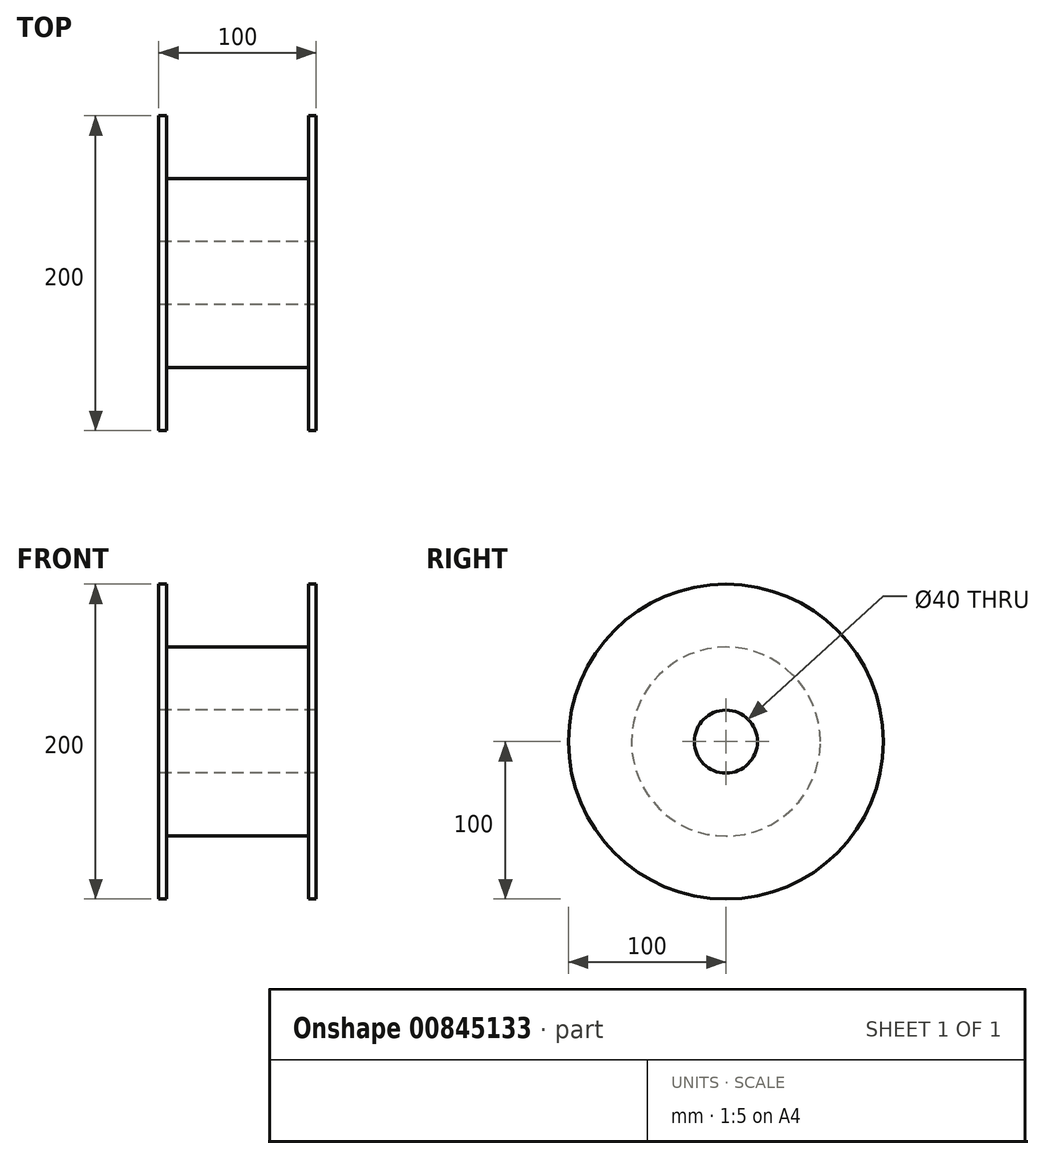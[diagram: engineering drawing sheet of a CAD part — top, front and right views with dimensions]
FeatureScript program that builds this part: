
annotation { "Feature Type Name" : "Feature", "Feature Type Description" : "" }
export const myFeature = defineFeature(function(context is Context, id is Id, definition is map)
    precondition{}
    {
        {
            var Q0;
            Q0=qCreatedBy(makeId("Right.planeOp"),FACE);
            var sketch = newSketch(context, id + "F0", { "sketchPlane" : qUnion([Q0])});
            skCircle(sketch, "E0", {"center": v(0, 0) * mm, "radius": 100 * mm});
            skCircle(sketch, "E1", {"center": v(0, 0) * mm, "radius": 20 * mm});
            skSolve(sketch);
        }
        {
            var Q0;
            Q0=makeQuery(id+"F0.imprint","IMPRINT",FACE,{"disambiguationData":[TD([[makeQuery(id+"F0.imprint","IMPRINT",EDGE,{"derivedFrom":sQuery(id+"F0.wireOp",EDGE,"E0")}),1.0]])]});
            extrude(context, id + "F1", {"entities" : qUnion([Q0]), "depth" : 50 * mm, "offsetDistance" : 25 * mm, "hasSecondDirection" : true, "secondDirectionOppositeDirection" : true, "secondDirectionDepth" : 50 * mm});
        }
        {
            var Q0;
            Q0=qCreatedBy(makeId("Front.planeOp"),FACE);
            var sketch = newSketch(context, id + "F2", { "sketchPlane" : qUnion([Q0])});
            skLineSegment(sketch, "E2.bottom", {"start": v(45, 60) * mm, "end": v(-45, 60) * mm});
            skLineSegment(sketch, "E2.top", {"start": v(45, 100) * mm, "end": v(-45, 100) * mm});
            skLineSegment(sketch, "E2.left", {"start": v(45, 60) * mm, "end": v(45, 100) * mm});
            skLineSegment(sketch, "E2.right", {"start": v(-45, 60) * mm, "end": v(-45, 100) * mm});
            skPoint(sketch, "E2.middle", {"position": v(0, 80) * mm});
            skLineSegment(sketch, "E3", {"start": v(0, 0) * mm, "end": v(-30, 0) * mm});
            skSolve(sketch);
        }
        {
            var Q0;
            Q0 = qSketchRegion(id + "F2", true);
            var Q1;
            Q1=sQuery(id+"F2.wireOp",EDGE,"E3");
            revolve(context, id + "F3", {"operationType" : NewBodyOperationType.REMOVE, "surfaceOperationType" : NewSurfaceOperationType.NEW, "entities" : qUnion([Q0]), "axis" : qUnion([Q1]), "revolveType" : RevolveType.FULL, "oppositeDirection" : true});
        }
    });
